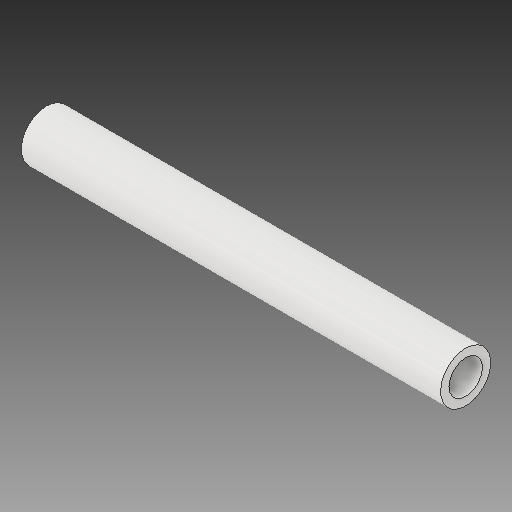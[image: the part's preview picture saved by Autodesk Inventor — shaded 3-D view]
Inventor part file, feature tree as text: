
AUTODESK INVENTOR PART (.ipt)
format: ipt  version: 2017.3 (Build 213256000, 256)  size: 92,672 bytes
history: native  units: mm
features: extrude x1, sketch x1
ambient origin geometry x8: Origin, YZ Plane, XZ Plane, XY Plane, X Axis, Y Axis, Z Axis, Center Point
bodies: Body1 (feature_tree)
feature tree (2):
  extrude  "Extrusion3"  Depth=20.0mm
  sketch  "Sketch4"  dims[d12=2.39mm d13=1.6mm d14=20.0mm d15=0.0mm]
